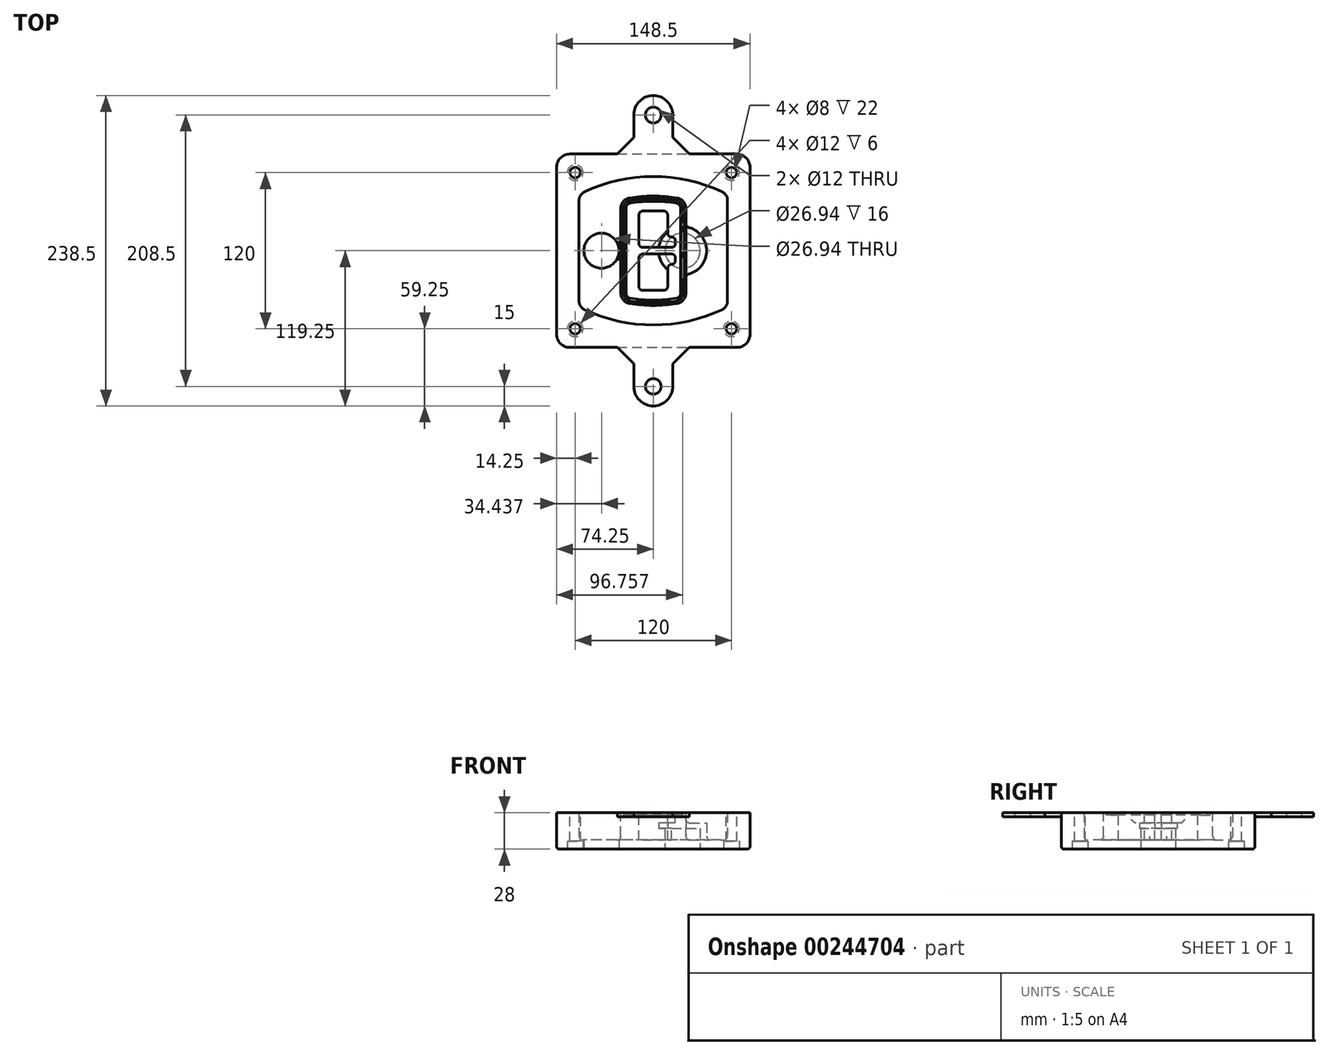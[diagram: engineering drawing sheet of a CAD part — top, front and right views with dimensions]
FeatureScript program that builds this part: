
annotation { "Feature Type Name" : "Feature", "Feature Type Description" : "" }
export const myFeature = defineFeature(function(context is Context, id is Id, definition is map)
    precondition{}
    {
        {
            var Q0;
            Q0=qCreatedBy(makeId("Top.planeOp"),FACE);
            var sketch = newSketch(context, id + "F0", { "sketchPlane" : qUnion([Q0])});
            skPoint(sketch, "E0.rect.middle", {"position": v(0, 0) * mm});
            skLineSegment(sketch, "E1.bottom", {"start": v(-64.25, -74.25) * mm, "end": v(64.25, -74.25) * mm});
            skLineSegment(sketch, "E1.top", {"start": v(-64.25, 74.25) * mm, "end": v(64.25, 74.25) * mm});
            skLineSegment(sketch, "E1.left", {"start": v(-74.25, -64.25) * mm, "end": v(-74.25, 64.25) * mm});
            skLineSegment(sketch, "E1.right", {"start": v(74.25, -64.25) * mm, "end": v(74.25, 64.25) * mm});
            skLineSegment(sketch, "E2", {"start": v(-74.25, 74.25) * mm, "end": v(74.25, -74.25) * mm, "construction": true});
            skLineSegment(sketch, "E3", {"start": v(74.25, 74.25) * mm, "end": v(-74.25, -74.25) * mm, "construction": true});
            skCircle(sketch, "E4", {"center": v(-60, 60) * mm, "radius": 4 * mm});
            skCircle(sketch, "E5", {"center": v(60, 60) * mm, "radius": 4 * mm});
            skCircle(sketch, "E6", {"center": v(60, -60) * mm, "radius": 4 * mm});
            skCircle(sketch, "E7", {"center": v(-60, -60) * mm, "radius": 4 * mm});
            skLineSegment(sketch, "E8", {"start": v(-60, 60) * mm, "end": v(60, 60) * mm, "construction": true});
            skLineSegment(sketch, "E9", {"start": v(60, 60) * mm, "end": v(60, -60) * mm, "construction": true});
            skLineSegment(sketch, "E10", {"start": v(60, -60) * mm, "end": v(-60, -60) * mm, "construction": true});
            skLineSegment(sketch, "E11", {"start": v(-60, -60) * mm, "end": v(-60, 60) * mm, "construction": true});
            skLineSegment(sketch, "E12", {"start": v(-60, 38.83) * mm, "end": v(-60, -38.83) * mm});
            skLineSegment(sketch, "E13", {"start": v(60, 38.83) * mm, "end": v(60, -38.83) * mm});
            skArc(sketch, "E14", {"start": v(54.26, 47.88) * mm, "mid": v(0, 60) * mm, "end": v(-54.26, 47.88) * mm});
            skArc(sketch, "E15", {"start": v(-54.26, -47.88) * mm, "mid": v(0, -60) * mm, "end": v(54.26, -47.88) * mm});
            skLineSegment(sketch, "E16", {"start": v(-60, 0) * mm, "end": v(60, 0) * mm, "construction": true});
            skPoint(sketch, "E17.visualSharp", {"position": v(-60, -45) * mm});
            skArc(sketch, "E17.filletArc", {"start": v(-60, -38.83) * mm, "mid": v(-58.44, -44.2) * mm, "end": v(-54.26, -47.88) * mm});
            skPoint(sketch, "E18.visualSharp", {"position": v(-60, 45) * mm});
            skArc(sketch, "E18.filletArc", {"start": v(-54.26, 47.88) * mm, "mid": v(-58.44, 44.2) * mm, "end": v(-60, 38.83) * mm});
            skPoint(sketch, "E19.visualSharp", {"position": v(60, 45) * mm});
            skArc(sketch, "E19.filletArc", {"start": v(60, 38.83) * mm, "mid": v(58.44, 44.2) * mm, "end": v(54.26, 47.88) * mm});
            skPoint(sketch, "E20.visualSharp", {"position": v(60, -45) * mm});
            skArc(sketch, "E20.filletArc", {"start": v(54.26, -47.88) * mm, "mid": v(58.44, -44.2) * mm, "end": v(60, -38.83) * mm});
            skPoint(sketch, "E21.visualSharp", {"position": v(-74.25, 74.25) * mm});
            skArc(sketch, "E21.filletArc", {"start": v(-64.25, 74.25) * mm, "mid": v(-71.32, 71.32) * mm, "end": v(-74.25, 64.25) * mm});
            skPoint(sketch, "E22.visualSharp", {"position": v(74.25, 74.25) * mm});
            skArc(sketch, "E22.filletArc", {"start": v(74.25, 64.25) * mm, "mid": v(71.32, 71.32) * mm, "end": v(64.25, 74.25) * mm});
            skPoint(sketch, "E23.visualSharp", {"position": v(74.25, -74.25) * mm});
            skArc(sketch, "E23.filletArc", {"start": v(64.25, -74.25) * mm, "mid": v(71.32, -71.32) * mm, "end": v(74.25, -64.25) * mm});
            skPoint(sketch, "E24.visualSharp", {"position": v(-74.25, -74.25) * mm});
            skArc(sketch, "E24.filletArc", {"start": v(-74.25, -64.25) * mm, "mid": v(-71.32, -71.32) * mm, "end": v(-64.25, -74.25) * mm});
            skArc(sketch, "E25.0", {"start": v(57, 38.83) * mm, "mid": v(55.9, 42.58) * mm, "end": v(52.98, 45.17) * mm});
            skLineSegment(sketch, "E25.1", {"start": v(57, 38.83) * mm, "end": v(57, -38.83) * mm});
            skArc(sketch, "E25.2", {"start": v(52.98, -45.17) * mm, "mid": v(55.9, -42.58) * mm, "end": v(57, -38.83) * mm});
            skArc(sketch, "E25.3", {"start": v(-52.98, -45.17) * mm, "mid": v(0, -57) * mm, "end": v(52.98, -45.17) * mm});
            skArc(sketch, "E25.4", {"start": v(-57, -38.83) * mm, "mid": v(-55.9, -42.58) * mm, "end": v(-52.98, -45.17) * mm});
            skArc(sketch, "E25.5", {"start": v(52.98, 45.17) * mm, "mid": v(0, 57) * mm, "end": v(-52.98, 45.17) * mm});
            skLineSegment(sketch, "E25.6", {"start": v(-57, 38.83) * mm, "end": v(-57, -38.83) * mm});
            skArc(sketch, "E25.7", {"start": v(-52.98, 45.17) * mm, "mid": v(-55.9, 42.58) * mm, "end": v(-57, 38.83) * mm});
            skArc(sketch, "E26.0", {"start": v(-55.96, 51.5) * mm, "mid": v(-61.82, 46.33) * mm, "end": v(-64, 38.83) * mm});
            skArc(sketch, "E26.1", {"start": v(55.96, 51.5) * mm, "mid": v(0, 64) * mm, "end": v(-55.96, 51.5) * mm});
            skArc(sketch, "E26.2", {"start": v(64, 38.83) * mm, "mid": v(61.82, 46.33) * mm, "end": v(55.96, 51.5) * mm});
            skLineSegment(sketch, "E26.3", {"start": v(64, 38.83) * mm, "end": v(64, -38.83) * mm});
            skArc(sketch, "E26.4", {"start": v(55.96, -51.5) * mm, "mid": v(61.82, -46.33) * mm, "end": v(64, -38.83) * mm});
            skLineSegment(sketch, "E26.5", {"start": v(-64, 38.83) * mm, "end": v(-64, -38.83) * mm});
            skArc(sketch, "E26.6", {"start": v(-55.96, -51.5) * mm, "mid": v(0, -64) * mm, "end": v(55.96, -51.5) * mm});
            skArc(sketch, "E26.7", {"start": v(-64, -38.83) * mm, "mid": v(-61.82, -46.33) * mm, "end": v(-55.96, -51.5) * mm});
            skSolve(sketch);
        }
        {
            var Q0;
            Q0=makeQuery(id+"F0.imprint","IMPRINT",FACE,{"disambiguationData":[TD([[makeQuery(id+"F0.imprint","IMPRINT",EDGE,{"derivedFrom":sQuery(id+"F0.wireOp",EDGE,"E1.bottom")}),1.0]])]});
            var Q1;
            Q1=makeQuery(id+"F0.imprint","IMPRINT",FACE,{"disambiguationData":[TD([[makeQuery(id+"F0.imprint","IMPRINT",EDGE,{"derivedFrom":sQuery(id+"F0.wireOp",EDGE,"E12")}),1.0]])]});
            var Q2;
            Q2=makeQuery(id+"F0.imprint","IMPRINT",FACE,{"disambiguationData":[TD([[makeQuery(id+"F0.imprint","IMPRINT",EDGE,{"derivedFrom":sQuery(id+"F0.wireOp",EDGE,"E25.0")}),1.0]])]});
            var Q3;
            Q3=makeQuery(id+"F0.imprint","IMPRINT",FACE,{"disambiguationData":[TD([[makeQuery(id+"F0.imprint","IMPRINT",EDGE,{"derivedFrom":sQuery(id+"F0.wireOp",EDGE,"E12")}),-1.0]])]});
            extrude(context, id + "F1", {"entities" : qUnion([Q0, Q1, Q2, Q3]), "oppositeDirection" : true, "depth" : 25 * mm});
        }
        {
            var Q0;
            Q0=makeQuery(id+"F0.imprint","IMPRINT",FACE,{"disambiguationData":[TD([[makeQuery(id+"F0.imprint","IMPRINT",EDGE,{"derivedFrom":sQuery(id+"F0.wireOp",EDGE,"E12")}),1.0]])]});
            extrude(context, id + "F2", {"entities" : qUnion([Q0]), "operationType" : NewBodyOperationType.ADD, "depth" : 3 * mm});
        }
        {
            var Q0;
            Q0=makeQuery(id+"F0.imprint","IMPRINT",FACE,{"disambiguationData":[TD([[makeQuery(id+"F0.imprint","IMPRINT",EDGE,{"derivedFrom":sQuery(id+"F0.wireOp",EDGE,"E25.0")}),1.0]])]});
            extrude(context, id + "F3", {"entities" : qUnion([Q0]), "operationType" : NewBodyOperationType.REMOVE, "oppositeDirection" : true, "depth" : 18 * mm});
        }
        {
            var Q0;
            Q0=makeQuery(id+"F2.opExtrude","CAP_FACE",FACE,{"disambiguationData":[OSD([sQuery(id+"F0.wireOp",EDGE,"E12"),sQuery(id+"F0.wireOp",EDGE,"E13"),sQuery(id+"F0.wireOp",EDGE,"E14"),sQuery(id+"F0.wireOp",EDGE,"E15"),sQuery(id+"F0.wireOp",EDGE,"E17.filletArc"),sQuery(id+"F0.wireOp",EDGE,"E18.filletArc"),sQuery(id+"F0.wireOp",EDGE,"E19.filletArc"),sQuery(id+"F0.wireOp",EDGE,"E20.filletArc"),sQuery(id+"F0.wireOp",EDGE,"E25.0"),sQuery(id+"F0.wireOp",EDGE,"E25.1"),sQuery(id+"F0.wireOp",EDGE,"E25.2"),sQuery(id+"F0.wireOp",EDGE,"E25.3"),sQuery(id+"F0.wireOp",EDGE,"E25.4"),sQuery(id+"F0.wireOp",EDGE,"E25.5"),sQuery(id+"F0.wireOp",EDGE,"E25.6"),sQuery(id+"F0.wireOp",EDGE,"E25.7")])],"isStart":false});
            var sketch = newSketch(context, id + "F4", { "sketchPlane" : qUnion([Q0])});
            skArc(sketch, "E27.0", {"start": v(-18.34, -40.45) * mm, "mid": v(0, -42) * mm, "end": v(18.34, -40.45) * mm});
            skArc(sketch, "E28.0", {"start": v(18.34, 40.45) * mm, "mid": v(0, 42) * mm, "end": v(-18.34, 40.45) * mm});
            skLineSegment(sketch, "E29", {"start": v(-25, 32.57) * mm, "end": v(-25, -32.57) * mm});
            skLineSegment(sketch, "E30", {"start": v(25, 32.57) * mm, "end": v(25, -32.57) * mm});
            skLineSegment(sketch, "E31", {"start": v(-25, 39.1) * mm, "end": v(25, 39.1) * mm, "construction": true});
            skLineSegment(sketch, "E32", {"start": v(-25, -39.1) * mm, "end": v(25, -39.1) * mm, "construction": true});
            skPoint(sketch, "E33.visualSharp", {"position": v(-25, 39.1) * mm});
            skArc(sketch, "E33.filletArc", {"start": v(-18.34, 40.45) * mm, "mid": v(-23.11, 37.73) * mm, "end": v(-25, 32.57) * mm});
            skPoint(sketch, "E34.visualSharp", {"position": v(25, 39.1) * mm});
            skArc(sketch, "E34.filletArc", {"start": v(25, 32.57) * mm, "mid": v(23.11, 37.73) * mm, "end": v(18.34, 40.45) * mm});
            skPoint(sketch, "E35.visualSharp", {"position": v(25, -39.1) * mm});
            skArc(sketch, "E35.filletArc", {"start": v(18.34, -40.45) * mm, "mid": v(23.11, -37.73) * mm, "end": v(25, -32.57) * mm});
            skPoint(sketch, "E36.visualSharp", {"position": v(-25, -39.1) * mm});
            skArc(sketch, "E36.filletArc", {"start": v(-25, -32.57) * mm, "mid": v(-23.11, -37.73) * mm, "end": v(-18.34, -40.45) * mm});
            skArc(sketch, "E37.0", {"start": v(52.98, 45.17) * mm, "mid": v(0, 57) * mm, "end": v(-52.98, 45.17) * mm});
            skArc(sketch, "E37.1", {"start": v(-52.98, 45.17) * mm, "mid": v(-55.9, 42.58) * mm, "end": v(-57, 38.83) * mm});
            skLineSegment(sketch, "E37.2", {"start": v(-57, 38.83) * mm, "end": v(-57, -38.83) * mm});
            skArc(sketch, "E37.3", {"start": v(-57, -38.83) * mm, "mid": v(-55.9, -42.58) * mm, "end": v(-52.98, -45.17) * mm});
            skArc(sketch, "E37.4", {"start": v(-52.98, -45.17) * mm, "mid": v(0, -57) * mm, "end": v(52.98, -45.17) * mm});
            skArc(sketch, "E37.5", {"start": v(52.98, -45.17) * mm, "mid": v(55.9, -42.58) * mm, "end": v(57, -38.83) * mm});
            skLineSegment(sketch, "E37.6", {"start": v(57, 38.83) * mm, "end": v(57, -38.83) * mm});
            skArc(sketch, "E37.7", {"start": v(57, 38.83) * mm, "mid": v(55.9, 42.58) * mm, "end": v(52.98, 45.17) * mm});
            skLineSegment(sketch, "E38.0", {"start": v(23, 32.57) * mm, "end": v(23, -32.57) * mm});
            skArc(sketch, "E38.1", {"start": v(18, -38.48) * mm, "mid": v(21.58, -36.44) * mm, "end": v(23, -32.57) * mm});
            skArc(sketch, "E38.2", {"start": v(-18, -38.48) * mm, "mid": v(0, -40) * mm, "end": v(18, -38.48) * mm});
            skArc(sketch, "E38.3", {"start": v(-23, -32.57) * mm, "mid": v(-21.58, -36.44) * mm, "end": v(-18, -38.48) * mm});
            skLineSegment(sketch, "E38.4", {"start": v(-23, 32.57) * mm, "end": v(-23, -32.57) * mm});
            skArc(sketch, "E38.5", {"start": v(23, 32.57) * mm, "mid": v(21.58, 36.44) * mm, "end": v(18, 38.48) * mm});
            skArc(sketch, "E38.6", {"start": v(-18, 38.48) * mm, "mid": v(-21.58, 36.44) * mm, "end": v(-23, 32.57) * mm});
            skArc(sketch, "E38.7", {"start": v(18, 38.48) * mm, "mid": v(0, 40) * mm, "end": v(-18, 38.48) * mm});
            skArc(sketch, "E39.0", {"start": v(21, 32.57) * mm, "mid": v(20.06, 35.15) * mm, "end": v(17.67, 36.5) * mm});
            skLineSegment(sketch, "E39.1", {"start": v(21, 32.57) * mm, "end": v(21, -32.57) * mm});
            skArc(sketch, "E39.2", {"start": v(17.67, -36.5) * mm, "mid": v(20.06, -35.15) * mm, "end": v(21, -32.57) * mm});
            skArc(sketch, "E39.3", {"start": v(-17.67, -36.5) * mm, "mid": v(0, -38) * mm, "end": v(17.67, -36.5) * mm});
            skArc(sketch, "E39.4", {"start": v(-21, -32.57) * mm, "mid": v(-20.06, -35.15) * mm, "end": v(-17.67, -36.5) * mm});
            skArc(sketch, "E39.5", {"start": v(17.67, 36.5) * mm, "mid": v(0, 38) * mm, "end": v(-17.67, 36.5) * mm});
            skLineSegment(sketch, "E39.6", {"start": v(-21, 32.57) * mm, "end": v(-21, -32.57) * mm});
            skArc(sketch, "E39.7", {"start": v(-17.67, 36.5) * mm, "mid": v(-20.06, 35.15) * mm, "end": v(-21, 32.57) * mm});
            skLineSegment(sketch, "E40", {"start": v(-25, 0) * mm, "end": v(25, 0) * mm, "construction": true});
            skLineSegment(sketch, "E41", {"start": v(-11, 5.5) * mm, "end": v(-11, 27.5) * mm});
            skLineSegment(sketch, "E42", {"start": v(-8, 30.5) * mm, "end": v(8, 30.5) * mm});
            skLineSegment(sketch, "E43", {"start": v(11, 27.5) * mm, "end": v(11, 13.5) * mm});
            skLineSegment(sketch, "E44", {"start": v(14, 10.5) * mm, "end": v(14, 10.5) * mm});
            skLineSegment(sketch, "E45", {"start": v(17, 7.5) * mm, "end": v(17, 5.5) * mm});
            skLineSegment(sketch, "E46", {"start": v(14, 2.5) * mm, "end": v(-8, 2.5) * mm});
            skPoint(sketch, "E47.visualSharp", {"position": v(-11, 30.5) * mm});
            skArc(sketch, "E47.filletArc", {"start": v(-8, 30.5) * mm, "mid": v(-10.12, 29.62) * mm, "end": v(-11, 27.5) * mm});
            skPoint(sketch, "E48.visualSharp", {"position": v(11, 30.5) * mm});
            skArc(sketch, "E48.filletArc", {"start": v(11, 27.5) * mm, "mid": v(10.12, 29.62) * mm, "end": v(8, 30.5) * mm});
            skPoint(sketch, "E49.visualSharp", {"position": v(11, 10.5) * mm});
            skArc(sketch, "E49.filletArc", {"start": v(11, 13.5) * mm, "mid": v(11.88, 11.38) * mm, "end": v(14, 10.5) * mm});
            skPoint(sketch, "E50.visualSharp", {"position": v(17, 10.5) * mm});
            skArc(sketch, "E50.filletArc", {"start": v(17, 7.5) * mm, "mid": v(16.12, 9.62) * mm, "end": v(14, 10.5) * mm});
            skPoint(sketch, "E51.visualSharp", {"position": v(17, 2.5) * mm});
            skArc(sketch, "E51.filletArc", {"start": v(14, 2.5) * mm, "mid": v(16.12, 3.38) * mm, "end": v(17, 5.5) * mm});
            skPoint(sketch, "E52.visualSharp", {"position": v(-11, 2.5) * mm});
            skArc(sketch, "E52.filletArc", {"start": v(-11, 5.5) * mm, "mid": v(-10.12, 3.38) * mm, "end": v(-8, 2.5) * mm});
            skLineSegment(sketch, "E53.0.MirrorCS", {"start": v(14, -2.5) * mm, "end": v(-8, -2.5) * mm});
            skArc(sketch, "E54.0.MirrorCS", {"start": v(-11, -5.5) * mm, "mid": v(-10.12, -3.38) * mm, "end": v(-8, -2.5) * mm});
            skLineSegment(sketch, "E55.0.MirrorCS", {"start": v(-11, -5.5) * mm, "end": v(-11, -27.5) * mm});
            skArc(sketch, "E56.0.MirrorCS", {"start": v(-8, -30.5) * mm, "mid": v(-10.12, -29.62) * mm, "end": v(-11, -27.5) * mm});
            skLineSegment(sketch, "E57.0.MirrorCS", {"start": v(-8, -30.5) * mm, "end": v(8, -30.5) * mm});
            skArc(sketch, "E58.0.MirrorCS", {"start": v(11, -27.5) * mm, "mid": v(10.12, -29.62) * mm, "end": v(8, -30.5) * mm});
            skLineSegment(sketch, "E59.0.MirrorCS", {"start": v(11, -27.5) * mm, "end": v(11, -13.5) * mm});
            skArc(sketch, "E60.0.MirrorCS", {"start": v(11, -13.5) * mm, "mid": v(11.88, -11.38) * mm, "end": v(14, -10.5) * mm});
            skArc(sketch, "E61.0.MirrorCS", {"start": v(17, -7.5) * mm, "mid": v(16.12, -9.62) * mm, "end": v(14, -10.5) * mm});
            skLineSegment(sketch, "E62.0.MirrorCS", {"start": v(17, -7.5) * mm, "end": v(17, -5.5) * mm});
            skArc(sketch, "E63.0.MirrorCS", {"start": v(14, -2.5) * mm, "mid": v(16.12, -3.38) * mm, "end": v(17, -5.5) * mm});
            skSolve(sketch);
        }
        {
            var Q0;
            Q0=makeQuery(id+"F4.imprint","IMPRINT",FACE,{"disambiguationData":[TD([[makeQuery(id+"F4.imprint","IMPRINT",EDGE,{"derivedFrom":sQuery(id+"F4.wireOp",EDGE,"E27.0")}),1.0]])]});
            var Q1;
            Q1=makeQuery(id+"F4.imprint","IMPRINT",FACE,{"disambiguationData":[TD([[makeQuery(id+"F4.imprint","IMPRINT",EDGE,{"derivedFrom":sQuery(id+"F4.wireOp",EDGE,"E38.0")}),-1.0]])]});
            var Q2;
            Q2=makeQuery(id+"F4.imprint","IMPRINT",FACE,{"disambiguationData":[TD([[makeQuery(id+"F4.imprint","IMPRINT",EDGE,{"derivedFrom":sQuery(id+"F4.wireOp",EDGE,"E39.0")}),1.0]])]});
            extrude(context, id + "F5", {"entities" : qUnion([Q0, Q1, Q2]), "operationType" : NewBodyOperationType.ADD, "endBound" : BoundingType.UP_TO_NEXT, "oppositeDirection" : true, "depth" : 25 * mm});
        }
        {
            var Q0;
            Q0=makeQuery(id+"F4.imprint","IMPRINT",FACE,{"disambiguationData":[TD([[makeQuery(id+"F4.imprint","IMPRINT",EDGE,{"derivedFrom":sQuery(id+"F4.wireOp",EDGE,"E38.0")}),-1.0]])]});
            extrude(context, id + "F6", {"entities" : qUnion([Q0]), "operationType" : NewBodyOperationType.REMOVE, "oppositeDirection" : true, "depth" : 2 * mm});
        }
        {
            var Q0;
            Q0=makeQuery(id+"F1.opExtrude","CAP_FACE",FACE,{"disambiguationData":[OSD([sQuery(id+"F0.wireOp",EDGE,"E1.bottom"),sQuery(id+"F0.wireOp",EDGE,"E1.top"),sQuery(id+"F0.wireOp",EDGE,"E1.left"),sQuery(id+"F0.wireOp",EDGE,"E1.right"),sQuery(id+"F0.wireOp",EDGE,"E4"),sQuery(id+"F0.wireOp",EDGE,"E5"),sQuery(id+"F0.wireOp",EDGE,"E6"),sQuery(id+"F0.wireOp",EDGE,"E7"),sQuery(id+"F0.wireOp",EDGE,"E21.filletArc"),sQuery(id+"F0.wireOp",EDGE,"E22.filletArc"),sQuery(id+"F0.wireOp",EDGE,"E23.filletArc"),sQuery(id+"F0.wireOp",EDGE,"E24.filletArc")])],"isStart":false});
            var sketch = newSketch(context, id + "F7", { "sketchPlane" : qUnion([Q0])});
            skCircle(sketch, "E64", {"center": v(22.5, 0) * mm, "radius": 13.47 * mm});
            skCircle(sketch, "E65", {"center": v(-39.81, 0) * mm, "radius": 13.47 * mm});
            skLineSegment(sketch, "E66", {"start": v(74.25, 0) * mm, "end": v(-74.25, 0) * mm});
            skCircle(sketch, "E67", {"center": v(22.5, 0) * mm, "radius": 18.47 * mm});
            skCircle(sketch, "E68", {"center": v(60, -60) * mm, "radius": 6 * mm});
            skCircle(sketch, "E69", {"center": v(-60, -60) * mm, "radius": 6 * mm});
            skCircle(sketch, "E70", {"center": v(-60, 60) * mm, "radius": 6 * mm});
            skCircle(sketch, "E71", {"center": v(60, 60) * mm, "radius": 6 * mm});
            skSolve(sketch);
        }
        {
            var Q0;
            {var subQ1=sQuery(id+"F7.wireOp",EDGE,"E66");var subQ4=sQuery(id+"F7.wireOp",EDGE,"E64");var subQ6=makeQuery(id+"F7.imprint","INTERSECT",VERTEX,{"disambiguationData":[OD(0.0)],"derivedFrom":[subQ4,subQ1]});Q0=makeQuery(id+"F7.imprint","IMPRINT",FACE,{"disambiguationData":[TD([[makeQuery(id+"F7.imprint","IMPRINT",EDGE,{"disambiguationData":[TD([[subQ6,-1.0]])],"derivedFrom":subQ4}),-1.0]])]});}
            var Q1;
            {var subQ0=sQuery(id+"F7.wireOp",EDGE,"E66");var subQ1=sQuery(id+"F7.wireOp",EDGE,"E64");var subQ3=makeQuery(id+"F7.imprint","INTERSECT",VERTEX,{"disambiguationData":[OD(0.0)],"derivedFrom":[subQ1,subQ0]});Q1=makeQuery(id+"F7.imprint","IMPRINT",FACE,{"disambiguationData":[TD([[makeQuery(id+"F7.imprint","IMPRINT",EDGE,{"disambiguationData":[TD([[subQ3,-1.0]])],"derivedFrom":subQ1}),1.0]])]});}
            var Q2;
            {var subQ0=sQuery(id+"F7.wireOp",EDGE,"E66");var subQ1=sQuery(id+"F7.wireOp",EDGE,"E64");var subQ3=makeQuery(id+"F7.imprint","INTERSECT",VERTEX,{"disambiguationData":[OD(0.0)],"derivedFrom":[subQ1,subQ0]});Q2=makeQuery(id+"F7.imprint","IMPRINT",FACE,{"disambiguationData":[TD([[makeQuery(id+"F7.imprint","IMPRINT",EDGE,{"disambiguationData":[TD([[subQ3,1.0]])],"derivedFrom":subQ1}),1.0]])]});}
            var Q3;
            {var subQ1=sQuery(id+"F7.wireOp",EDGE,"E66");var subQ4=sQuery(id+"F7.wireOp",EDGE,"E64");var subQ6=makeQuery(id+"F7.imprint","INTERSECT",VERTEX,{"disambiguationData":[OD(0.0)],"derivedFrom":[subQ4,subQ1]});Q3=makeQuery(id+"F7.imprint","IMPRINT",FACE,{"disambiguationData":[TD([[makeQuery(id+"F7.imprint","IMPRINT",EDGE,{"disambiguationData":[TD([[subQ6,1.0]])],"derivedFrom":subQ4}),-1.0]])]});}
            extrude(context, id + "F8", {"entities" : qUnion([Q0, Q1, Q2, Q3]), "operationType" : NewBodyOperationType.ADD, "oppositeDirection" : true, "depth" : 20 * mm});
        }
        {
            var Q0;
            {var subQ0=sQuery(id+"F7.wireOp",EDGE,"E66");var subQ1=sQuery(id+"F7.wireOp",EDGE,"E64");var subQ3=makeQuery(id+"F7.imprint","INTERSECT",VERTEX,{"disambiguationData":[OD(0.0)],"derivedFrom":[subQ1,subQ0]});Q0=makeQuery(id+"F7.imprint","IMPRINT",FACE,{"disambiguationData":[TD([[makeQuery(id+"F7.imprint","IMPRINT",EDGE,{"disambiguationData":[TD([[subQ3,-1.0]])],"derivedFrom":subQ1}),1.0]])]});}
            var Q1;
            {var subQ0=sQuery(id+"F7.wireOp",EDGE,"E66");var subQ1=sQuery(id+"F7.wireOp",EDGE,"E64");var subQ3=makeQuery(id+"F7.imprint","INTERSECT",VERTEX,{"disambiguationData":[OD(0.0)],"derivedFrom":[subQ1,subQ0]});Q1=makeQuery(id+"F7.imprint","IMPRINT",FACE,{"disambiguationData":[TD([[makeQuery(id+"F7.imprint","IMPRINT",EDGE,{"disambiguationData":[TD([[subQ3,1.0]])],"derivedFrom":subQ1}),1.0]])]});}
            extrude(context, id + "F9", {"entities" : qUnion([Q0, Q1]), "operationType" : NewBodyOperationType.REMOVE, "oppositeDirection" : true, "depth" : 16 * mm});
        }
        {
            var Q0;
            {var subQ0=sQuery(id+"F7.wireOp",EDGE,"E66");var subQ1=sQuery(id+"F7.wireOp",EDGE,"E65");var subQ3=makeQuery(id+"F7.imprint","INTERSECT",VERTEX,{"disambiguationData":[OD(0.0)],"derivedFrom":[subQ1,subQ0]});Q0=makeQuery(id+"F7.imprint","IMPRINT",FACE,{"disambiguationData":[TD([[makeQuery(id+"F7.imprint","IMPRINT",EDGE,{"disambiguationData":[TD([[subQ3,-1.0]])],"derivedFrom":subQ1}),1.0]])]});}
            var Q1;
            {var subQ0=sQuery(id+"F7.wireOp",EDGE,"E66");var subQ1=sQuery(id+"F7.wireOp",EDGE,"E65");var subQ3=makeQuery(id+"F7.imprint","INTERSECT",VERTEX,{"disambiguationData":[OD(0.0)],"derivedFrom":[subQ1,subQ0]});Q1=makeQuery(id+"F7.imprint","IMPRINT",FACE,{"disambiguationData":[TD([[makeQuery(id+"F7.imprint","IMPRINT",EDGE,{"disambiguationData":[TD([[subQ3,1.0]])],"derivedFrom":subQ1}),1.0]])]});}
            extrude(context, id + "F10", {"entities" : qUnion([Q0, Q1]), "operationType" : NewBodyOperationType.REMOVE, "oppositeDirection" : true, "depth" : 25 * mm});
        }
        {
            var Q0;
            Q0=makeQuery(id+"F7.imprint","IMPRINT",FACE,{"disambiguationData":[TD([[makeQuery(id+"F7.imprint","IMPRINT",EDGE,{"derivedFrom":sQuery(id+"F7.wireOp",EDGE,"E68")}),1.0]])]});
            var Q1;
            Q1=makeQuery(id+"F7.imprint","IMPRINT",FACE,{"disambiguationData":[TD([[makeQuery(id+"F7.imprint","IMPRINT",EDGE,{"derivedFrom":makeQuery(id+"F1.opExtrude","CAP_EDGE",EDGE,{"disambiguationData":[OSD([sQuery(id+"F0.wireOp",EDGE,"E5")])],"isStart":false})}),-1.0]])]});
            var Q2;
            Q2=makeQuery(id+"F7.imprint","IMPRINT",FACE,{"disambiguationData":[TD([[makeQuery(id+"F7.imprint","IMPRINT",EDGE,{"derivedFrom":sQuery(id+"F7.wireOp",EDGE,"E69")}),1.0]])]});
            var Q3;
            Q3=makeQuery(id+"F7.imprint","IMPRINT",FACE,{"disambiguationData":[TD([[makeQuery(id+"F7.imprint","IMPRINT",EDGE,{"derivedFrom":makeQuery(id+"F1.opExtrude","CAP_EDGE",EDGE,{"disambiguationData":[OSD([sQuery(id+"F0.wireOp",EDGE,"E4")])],"isStart":false})}),-1.0]])]});
            var Q4;
            Q4=makeQuery(id+"F7.imprint","IMPRINT",FACE,{"disambiguationData":[TD([[makeQuery(id+"F7.imprint","IMPRINT",EDGE,{"derivedFrom":sQuery(id+"F7.wireOp",EDGE,"E70")}),1.0]])]});
            var Q5;
            Q5=makeQuery(id+"F7.imprint","IMPRINT",FACE,{"disambiguationData":[TD([[makeQuery(id+"F7.imprint","IMPRINT",EDGE,{"derivedFrom":makeQuery(id+"F1.opExtrude","CAP_EDGE",EDGE,{"disambiguationData":[OSD([sQuery(id+"F0.wireOp",EDGE,"E7")])],"isStart":false})}),-1.0]])]});
            var Q6;
            Q6=makeQuery(id+"F7.imprint","IMPRINT",FACE,{"disambiguationData":[TD([[makeQuery(id+"F7.imprint","IMPRINT",EDGE,{"derivedFrom":sQuery(id+"F7.wireOp",EDGE,"E71")}),1.0]])]});
            var Q7;
            Q7=makeQuery(id+"F7.imprint","IMPRINT",FACE,{"disambiguationData":[TD([[makeQuery(id+"F7.imprint","IMPRINT",EDGE,{"derivedFrom":makeQuery(id+"F1.opExtrude","CAP_EDGE",EDGE,{"disambiguationData":[OSD([sQuery(id+"F0.wireOp",EDGE,"E6")])],"isStart":false})}),-1.0]])]});
            extrude(context, id + "F11", {"entities" : qUnion([Q0, Q1, Q2, Q3, Q4, Q5, Q6, Q7]), "operationType" : NewBodyOperationType.REMOVE, "oppositeDirection" : true, "depth" : 6 * mm});
        }
        {
            var Q0;
            Q0=makeQuery(id+"F9.boolean.opBoolean","COPY",FACE,{"derivedFrom":makeQuery(id+"F9.opExtrude","CAP_FACE",FACE,{"disambiguationData":[OSD([sQuery(id+"F7.wireOp",EDGE,"E64")])],"isStart":false})});
            var sketch = newSketch(context, id + "F12", { "sketchPlane" : qUnion([Q0])});
            skArc(sketch, "E72.0", {"start": v(11, 14.45) * mm, "mid": v(6.45, 9.13) * mm, "end": v(4.2, 2.5) * mm});
            skArc(sketch, "E72.1", {"start": v(4.2, -2.5) * mm, "mid": v(6.45, -9.13) * mm, "end": v(11, -14.45) * mm});
            skLineSegment(sketch, "E73", {"start": v(4.2, -2.5) * mm, "end": v(14, -2.5) * mm});
            skLineSegment(sketch, "E74.0", {"start": v(14, 2.5) * mm, "end": v(4.2, 2.5) * mm});
            skArc(sketch, "E74.1", {"start": v(14, 2.5) * mm, "mid": v(16.12, 3.38) * mm, "end": v(17, 5.5) * mm});
            skLineSegment(sketch, "E74.2", {"start": v(17, 7.5) * mm, "end": v(17, 5.5) * mm});
            skArc(sketch, "E74.3", {"start": v(17, 7.5) * mm, "mid": v(16.12, 9.62) * mm, "end": v(14, 10.5) * mm});
            skArc(sketch, "E74.4", {"start": v(11, 13.5) * mm, "mid": v(11.88, 11.38) * mm, "end": v(14, 10.5) * mm});
            skLineSegment(sketch, "E74.5", {"start": v(11, 14.45) * mm, "end": v(11, 13.5) * mm});
            skLineSegment(sketch, "E74.7", {"start": v(14, -2.5) * mm, "end": v(4.2, -2.5) * mm});
            skArc(sketch, "E74.8", {"start": v(14, -2.5) * mm, "mid": v(16.12, -3.38) * mm, "end": v(17, -5.5) * mm});
            skLineSegment(sketch, "E74.9", {"start": v(17, -7.5) * mm, "end": v(17, -5.5) * mm});
            skArc(sketch, "E74.10", {"start": v(17, -7.5) * mm, "mid": v(16.12, -9.62) * mm, "end": v(14, -10.5) * mm});
            skArc(sketch, "E74.11", {"start": v(11, -13.5) * mm, "mid": v(11.88, -11.38) * mm, "end": v(14, -10.5) * mm});
            skLineSegment(sketch, "E74.12", {"start": v(11, -14.45) * mm, "end": v(11, -13.5) * mm});
            skPoint(sketch, "E75.orphan", {"position": v(11, -27.5) * mm});
            skPoint(sketch, "E76.orphan", {"position": v(-8, -2.5) * mm});
            skPoint(sketch, "E77.orphan", {"position": v(-8, 2.5) * mm});
            skPoint(sketch, "E78.orphan", {"position": v(11, 27.5) * mm});
            skSolve(sketch);
        }
        {
            var Q0;
            {var subQ7=sQuery(id+"F12.wireOp",EDGE,"E72.0");var subQ14=sQuery(id+"F12.wireOp",EDGE,"E72.1");var subQ16=sQuery(id+"F12.wireOp",EDGE,"E74.1");var subQ18=sQuery(id+"F12.wireOp",EDGE,"E74.8");Q0=qUnion([makeQuery(id+"F12.imprint","IMPRINT",FACE,{"disambiguationData":[TD([[makeQuery(id+"F12.imprint","IMPRINT",EDGE,{"derivedFrom":subQ7}),1.0]])]}),makeQuery(id+"F12.imprint","IMPRINT",FACE,{"disambiguationData":[TD([[makeQuery(id+"F12.imprint","IMPRINT",EDGE,{"derivedFrom":subQ14}),1.0]])]}),makeQuery(id+"F12.imprint","IMPRINT",FACE,{"disambiguationData":[TD([[makeQuery(id+"F12.imprint","IMPRINT",EDGE,{"derivedFrom":subQ16}),1.0]])]}),makeQuery(id+"F12.imprint","IMPRINT",FACE,{"disambiguationData":[TD([[makeQuery(id+"F12.imprint","IMPRINT",EDGE,{"derivedFrom":subQ18}),-1.0]])]})]);}
            var Q1;
            Q1=makeQuery(id+"F5.boolean.opBoolean","SPLIT",FACE,{"disambiguationData":[TD([makeQuery(id+"F5.opExtrude","SWEPT_FACE",FACE,{"disambiguationData":[OSD([sQuery(id+"F4.wireOp",EDGE,"E41")])]})])],"derivedFrom":makeQuery(id+"F3.boolean.opBoolean","COPY",FACE,{"derivedFrom":makeQuery(id+"F3.opExtrude","CAP_FACE",FACE,{"disambiguationData":[OSD([sQuery(id+"F0.wireOp",EDGE,"E25.0"),sQuery(id+"F0.wireOp",EDGE,"E25.1"),sQuery(id+"F0.wireOp",EDGE,"E25.2"),sQuery(id+"F0.wireOp",EDGE,"E25.3"),sQuery(id+"F0.wireOp",EDGE,"E25.4"),sQuery(id+"F0.wireOp",EDGE,"E25.5"),sQuery(id+"F0.wireOp",EDGE,"E25.6"),sQuery(id+"F0.wireOp",EDGE,"E25.7")])],"isStart":false})})});
            extrude(context, id + "F13", {"entities" : qUnion([Q0]), "operationType" : NewBodyOperationType.REMOVE, "endBound" : BoundingType.UP_TO_SURFACE, "endBoundEntityFace" : qUnion([Q1]), "depth" : 25 * mm});
        }
        {
            var Q0;
            Q0=makeQuery(id+"F3.boolean.opBoolean","COPY",EDGE,{"derivedFrom":makeQuery(id+"F3.opExtrude","CAP_EDGE",EDGE,{"disambiguationData":[OSD([sQuery(id+"F0.wireOp",EDGE,"E25.6")])],"isStart":false})});
            var Q1;
            Q1=makeQuery(id+"F8.boolean.opBoolean","INTERSECT",EDGE,{"derivedFrom":[makeQuery(id+"F5.opExtrude","SWEPT_FACE",FACE,{"disambiguationData":[OSD([sQuery(id+"F4.wireOp",EDGE,"E30")])]}),makeQuery(id+"F8.opExtrude","CAP_FACE",FACE,{"disambiguationData":[OSD([sQuery(id+"F7.wireOp",EDGE,"E67")])],"isStart":false})]});
            var Q2;
            Q2=makeQuery(id+"F8.boolean.opBoolean","INTERSECT",EDGE,{"disambiguationData":[OD(1.0)],"derivedFrom":[makeQuery(id+"F5.opExtrude","SWEPT_FACE",FACE,{"disambiguationData":[OSD([sQuery(id+"F4.wireOp",EDGE,"E30")])]}),makeQuery(id+"F8.opExtrude","SWEPT_FACE",FACE,{"disambiguationData":[OSD([sQuery(id+"F7.wireOp",EDGE,"E67")])]})]});
            var Q3;
            {var subQ0=sQuery(id+"F4.wireOp",EDGE,"E30");Q3=makeQuery(id+"F8.boolean.opBoolean","SPLIT",EDGE,{"disambiguationData":[TD([makeQuery(id+"F5.opExtrude","SWEPT_FACE",FACE,{"disambiguationData":[OSD([sQuery(id+"F4.wireOp",EDGE,"E35.filletArc")])]})])],"derivedFrom":makeQuery(id+"F5.opExtrude","CAP_EDGE",EDGE,{"disambiguationData":[OSD([subQ0])],"isStart":false})});}
            var Q4;
            {var subQ0=sQuery(id+"F0.wireOp",EDGE,"E25.7");var subQ1=sQuery(id+"F0.wireOp",EDGE,"E25.1");var subQ2=sQuery(id+"F0.wireOp",EDGE,"E25.6");var subQ3=sQuery(id+"F0.wireOp",EDGE,"E25.5");var subQ4=sQuery(id+"F0.wireOp",EDGE,"E25.4");var subQ5=sQuery(id+"F0.wireOp",EDGE,"E25.0");var subQ6=sQuery(id+"F0.wireOp",EDGE,"E25.2");var subQ7=sQuery(id+"F0.wireOp",EDGE,"E25.3");Q4=makeQuery(id+"F8.boolean.opBoolean","INTERSECT",EDGE,{"derivedFrom":[makeQuery(id+"F5.boolean.opBoolean","SPLIT",FACE,{"disambiguationData":[TD([makeQuery(id+"F2.opExtrude","SWEPT_FACE",FACE,{"disambiguationData":[OSD([subQ5])]})])],"derivedFrom":makeQuery(id+"F3.boolean.opBoolean","COPY",FACE,{"derivedFrom":makeQuery(id+"F3.opExtrude","CAP_FACE",FACE,{"disambiguationData":[OSD([subQ5,subQ1,subQ6,subQ7,subQ4,subQ3,subQ2,subQ0])],"isStart":false})})}),makeQuery(id+"F8.opExtrude","SWEPT_FACE",FACE,{"disambiguationData":[OSD([sQuery(id+"F7.wireOp",EDGE,"E67")])]})]});}
            var Q5;
            Q5=makeQuery(id+"F8.boolean.opBoolean","INTERSECT",EDGE,{"disambiguationData":[OD(0.0)],"derivedFrom":[makeQuery(id+"F5.opExtrude","SWEPT_FACE",FACE,{"disambiguationData":[OSD([sQuery(id+"F4.wireOp",EDGE,"E30")])]}),makeQuery(id+"F8.opExtrude","SWEPT_FACE",FACE,{"disambiguationData":[OSD([sQuery(id+"F7.wireOp",EDGE,"E67")])]})]});
            fillet(context, id + "F14", {"entities" : qUnion([Q0, Q1, Q2, Q3, Q4, Q5]), "radius" : 3 * mm, "tangentPropagation" : true, "allowEdgeOverflow" : false});
        }
        {
            var Q0;
            Q0=makeQuery(id+"F1.opExtrude","CAP_EDGE",EDGE,{"disambiguationData":[OSD([sQuery(id+"F0.wireOp",EDGE,"E1.bottom")])],"isStart":false});
            fillet(context, id + "F15", {"entities" : qUnion([Q0]), "radius" : 2 * mm, "tangentPropagation" : true, "allowEdgeOverflow" : false});
        }
        {
            var Q0;
            {var subQ0=sQuery(id+"F0.wireOp",EDGE,"E22.filletArc");var subQ1=sQuery(id+"F0.wireOp",EDGE,"E7");var subQ2=sQuery(id+"F0.wireOp",EDGE,"E6");var subQ3=sQuery(id+"F0.wireOp",EDGE,"E5");var subQ4=sQuery(id+"F0.wireOp",EDGE,"E4");var subQ5=sQuery(id+"F0.wireOp",EDGE,"E1.bottom");var subQ6=sQuery(id+"F0.wireOp",EDGE,"E21.filletArc");var subQ7=sQuery(id+"F0.wireOp",EDGE,"E1.top");var subQ8=sQuery(id+"F0.wireOp",EDGE,"E1.left");var subQ9=sQuery(id+"F0.wireOp",EDGE,"E1.right");var subQ10=sQuery(id+"F0.wireOp",EDGE,"E23.filletArc");var subQ11=sQuery(id+"F0.wireOp",EDGE,"E24.filletArc");Q0=makeQuery(id+"F2.boolean.opBoolean","SPLIT",FACE,{"disambiguationData":[TD([makeQuery(id+"F1.opExtrude","SWEPT_FACE",FACE,{"disambiguationData":[OSD([subQ5])]})])],"derivedFrom":makeQuery(id+"F1.opExtrude","CAP_FACE",FACE,{"disambiguationData":[OSD([subQ5,subQ7,subQ8,subQ9,subQ4,subQ3,subQ2,subQ1,subQ6,subQ0,subQ10,subQ11])],"isStart":true})});}
            var sketch = newSketch(context, id + "F16", { "sketchPlane" : qUnion([Q0])});
            skLineSegment(sketch, "E79", {"start": v(-27.73, 74.25) * mm, "end": v(-15, 86.98) * mm});
            skLineSegment(sketch, "E80", {"start": v(-15, 86.98) * mm, "end": v(-15, 104.25) * mm});
            skLineSegment(sketch, "E81", {"start": v(27.73, 74.25) * mm, "end": v(15, 86.98) * mm});
            skLineSegment(sketch, "E82", {"start": v(15, 86.98) * mm, "end": v(15, 104.25) * mm});
            skCircle(sketch, "E83", {"center": v(0, 104.25) * mm, "radius": 6 * mm});
            skLineSegment(sketch, "E84", {"start": v(0, 0) * mm, "end": v(144.51, 0) * mm});
            skLineSegment(sketch, "E85.MirrorCS", {"start": v(27.73, -74.25) * mm, "end": v(15, -86.98) * mm});
            skLineSegment(sketch, "E86.MirrorCS", {"start": v(15, -86.98) * mm, "end": v(15, -104.25) * mm});
            skLineSegment(sketch, "E87.MirrorCS", {"start": v(-15, -86.98) * mm, "end": v(-15, -104.25) * mm});
            skCircle(sketch, "E88.MirrorC", {"center": v(0, -104.25) * mm, "radius": 6 * mm});
            skLineSegment(sketch, "E89.MirrorCS", {"start": v(-27.73, -74.25) * mm, "end": v(-15, -86.98) * mm});
            skArc(sketch, "E90", {"start": v(15, 104.25) * mm, "mid": v(0, 119.25) * mm, "end": v(-15, 104.25) * mm});
            skArc(sketch, "E91", {"start": v(-15, -104.25) * mm, "mid": v(0, -119.25) * mm, "end": v(15, -104.25) * mm});
            skSolve(sketch);
        }
        {
            var Q0;
            {var subQ3=sQuery(id+"F16.wireOp",EDGE,"E85.MirrorCS");Q0=makeQuery(id+"F16.imprint","IMPRINT",FACE,{"disambiguationData":[TD([[makeQuery(id+"F16.imprint","IMPRINT",EDGE,{"derivedFrom":subQ3}),-1.0]])]});}
            var Q1;
            Q1=makeQuery(id+"F16.imprint","IMPRINT",FACE,{"disambiguationData":[TD([[makeQuery(id+"F16.imprint","IMPRINT",EDGE,{"derivedFrom":makeQuery(id+"F1.opExtrude","CAP_EDGE",EDGE,{"disambiguationData":[OSD([sQuery(id+"F0.wireOp",EDGE,"E1.left")])],"isStart":true})}),-1.0]])]});
            var Q2;
            {var subQ4=sQuery(id+"F16.wireOp",EDGE,"E79");Q2=makeQuery(id+"F16.imprint","IMPRINT",FACE,{"disambiguationData":[TD([[makeQuery(id+"F16.imprint","IMPRINT",EDGE,{"derivedFrom":subQ4}),-1.0]])]});}
            var Q3;
            Q3=makeQuery(id+"F2.opExtrude","CAP_FACE",FACE,{"disambiguationData":[OSD([sQuery(id+"F0.wireOp",EDGE,"E12"),sQuery(id+"F0.wireOp",EDGE,"E13"),sQuery(id+"F0.wireOp",EDGE,"E14"),sQuery(id+"F0.wireOp",EDGE,"E15"),sQuery(id+"F0.wireOp",EDGE,"E17.filletArc"),sQuery(id+"F0.wireOp",EDGE,"E18.filletArc"),sQuery(id+"F0.wireOp",EDGE,"E19.filletArc"),sQuery(id+"F0.wireOp",EDGE,"E20.filletArc"),sQuery(id+"F0.wireOp",EDGE,"E25.0"),sQuery(id+"F0.wireOp",EDGE,"E25.1"),sQuery(id+"F0.wireOp",EDGE,"E25.2"),sQuery(id+"F0.wireOp",EDGE,"E25.3"),sQuery(id+"F0.wireOp",EDGE,"E25.4"),sQuery(id+"F0.wireOp",EDGE,"E25.5"),sQuery(id+"F0.wireOp",EDGE,"E25.6"),sQuery(id+"F0.wireOp",EDGE,"E25.7")])],"isStart":false});
            extrude(context, id + "F17", {"entities" : qUnion([Q0, Q1, Q2]), "operationType" : NewBodyOperationType.ADD, "endBound" : BoundingType.UP_TO_SURFACE, "endBoundEntityFace" : qUnion([Q3]), "depth" : 25 * mm});
        }
    });
